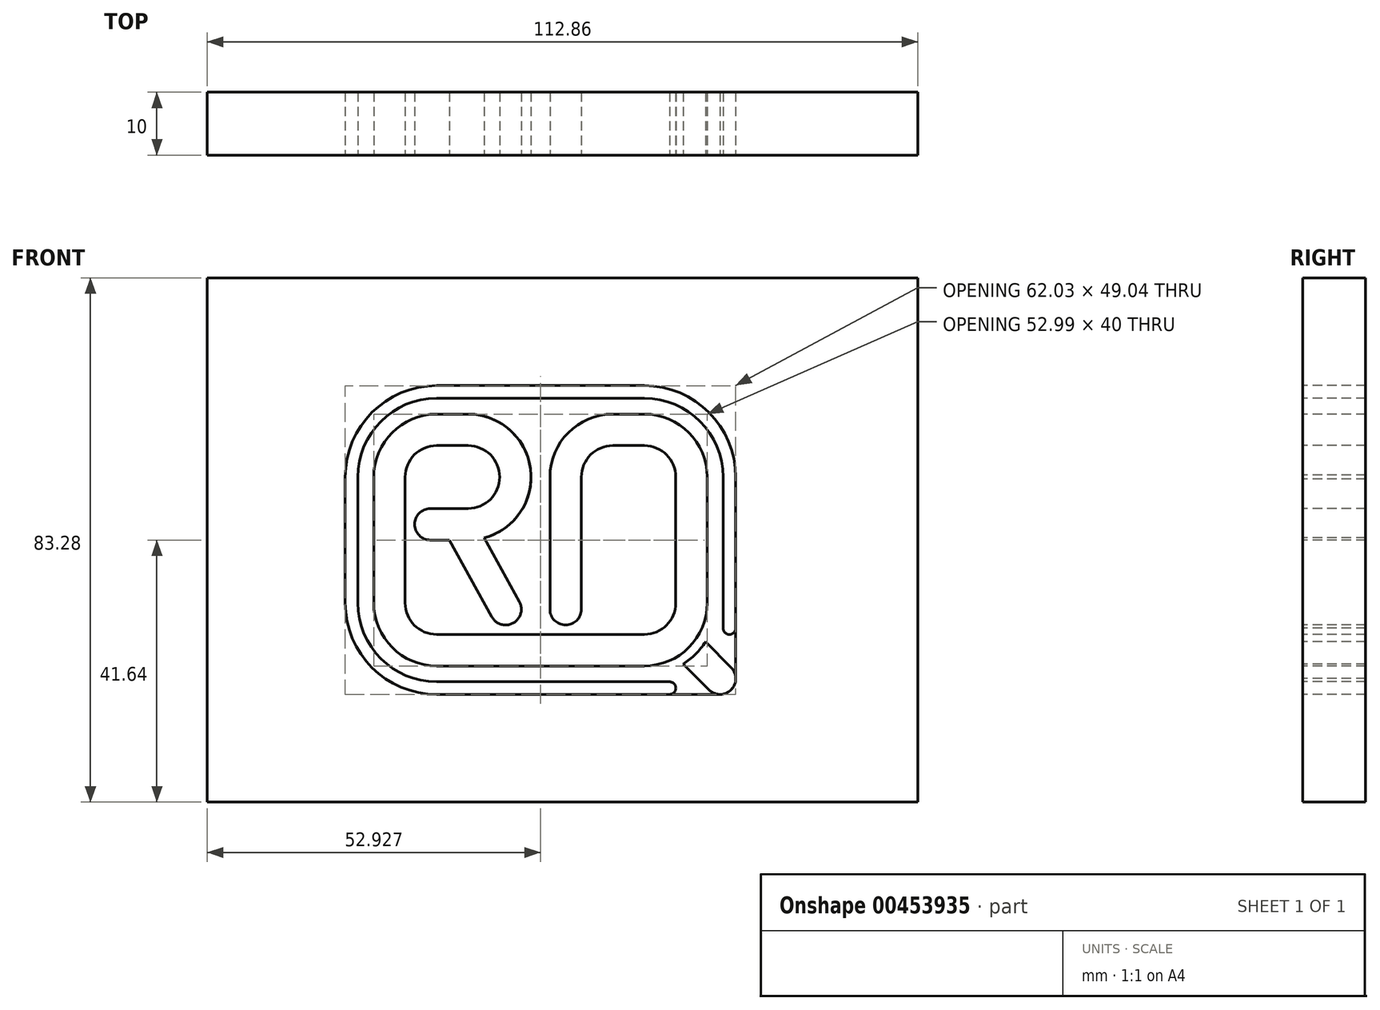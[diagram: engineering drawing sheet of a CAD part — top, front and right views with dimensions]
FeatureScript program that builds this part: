
annotation { "Feature Type Name" : "Feature", "Feature Type Description" : "" }
export const myFeature = defineFeature(function(context is Context, id is Id, definition is map)
    precondition{}
    {
        {
            var Q0;
            Q0=qCreatedBy(makeId("Front.planeOp"),FACE);
            var sketch = newSketch(context, id + "F0", { "sketchPlane" : qUnion([Q0])});
            skPoint(sketch, "E0.middle", {"position": v(0, 0) * mm});
            skLineSegment(sketch, "E1", {"start": v(-25, 10) * mm, "end": v(-25, -10) * mm});
            skLineSegment(sketch, "E2", {"start": v(-2, -20) * mm, "end": v(-0.38, -20) * mm});
            skLineSegment(sketch, "E3", {"start": v(-2, -11) * mm, "end": v(-2, 10) * mm});
            skLineSegment(sketch, "E4", {"start": v(8, 20) * mm, "end": v(13, 20) * mm});
            skLineSegment(sketch, "E5", {"start": v(23, 10) * mm, "end": v(23, -10) * mm});
            skLineSegment(sketch, "E6", {"start": v(13, -20) * mm, "end": v(9, -20) * mm});
            skLineSegment(sketch, "E7", {"start": v(-25, 20) * mm, "end": v(-15, 20) * mm});
            skLineSegment(sketch, "E8", {"start": v(-21, 0) * mm, "end": v(-15, 0) * mm});
            skLineSegment(sketch, "E9", {"start": v(-5, 10.33) * mm, "end": v(-5, 10.33) * mm});
            skPoint(sketch, "E10.visualSharp", {"position": v(-5.33, 20) * mm});
            skArc(sketch, "E10.filletArc", {"start": v(-5, 10.33) * mm, "mid": v(-8.05, 17.19) * mm, "end": v(-15, 20) * mm});
            skArc(sketch, "E11.filletArc", {"start": v(-15, 0) * mm, "mid": v(-7.81, 3.05) * mm, "end": v(-5, 10.33) * mm});
            skPoint(sketch, "E12.visualSharp", {"position": v(-3.63, -20) * mm});
            skPoint(sketch, "E13.visualSharp", {"position": v(23, -20) * mm});
            skArc(sketch, "E13.filletArc", {"start": v(13, -20) * mm, "mid": v(20.07, -17.07) * mm, "end": v(23, -10) * mm});
            skPoint(sketch, "E14.visualSharp", {"position": v(23, 20) * mm});
            skArc(sketch, "E14.filletArc", {"start": v(23, 10) * mm, "mid": v(20.07, 17.07) * mm, "end": v(13, 20) * mm});
            skPoint(sketch, "E15.visualSharp", {"position": v(-2, 20) * mm});
            skArc(sketch, "E15.filletArc", {"start": v(8, 20) * mm, "mid": v(0.92, 17.07) * mm, "end": v(-2, 10) * mm});
            skPoint(sketch, "E16.visualSharp", {"position": v(-2, -20) * mm});
            skArc(sketch, "E17.0", {"start": v(8, 15) * mm, "mid": v(4.46, 13.54) * mm, "end": v(3, 10) * mm});
            skLineSegment(sketch, "E17.1", {"start": v(3, -11) * mm, "end": v(3, 10) * mm});
            skLineSegment(sketch, "E17.2", {"start": v(8, 15) * mm, "end": v(13, 15) * mm});
            skArc(sketch, "E17.4", {"start": v(18, 10) * mm, "mid": v(16.53, 13.54) * mm, "end": v(13, 15) * mm});
            skLineSegment(sketch, "E17.5", {"start": v(18, 10) * mm, "end": v(18, -10) * mm});
            skArc(sketch, "E17.6", {"start": v(13, -15) * mm, "mid": v(16.53, -13.54) * mm, "end": v(18, -10) * mm});
            skLineSegment(sketch, "E17.7", {"start": v(13, -15) * mm, "end": v(9, -15) * mm});
            skArc(sketch, "E18.1", {"start": v(-15, 5) * mm, "mid": v(-11.44, 6.5) * mm, "end": v(-10, 10.08) * mm});
            skArc(sketch, "E18.2", {"start": v(-10, 10.08) * mm, "mid": v(-11.5, 13.56) * mm, "end": v(-15, 15) * mm});
            skLineSegment(sketch, "E18.3", {"start": v(-20, 15) * mm, "end": v(-15, 15) * mm});
            skLineSegment(sketch, "E19.0", {"start": v(-30, 17.5) * mm, "end": v(-30, -10) * mm});
            skLineSegment(sketch, "E20.0", {"start": v(-1, -15) * mm, "end": v(-0.38, -15) * mm});
            skLineSegment(sketch, "E21", {"start": v(-20, -20) * mm, "end": v(-2, -20) * mm});
            skLineSegment(sketch, "E22", {"start": v(-1, -15) * mm, "end": v(9, -15) * mm});
            skLineSegment(sketch, "E23.0", {"start": v(-20, -15) * mm, "end": v(0, -15) * mm});
            skLineSegment(sketch, "E24", {"start": v(-5, 10.33) * mm, "end": v(-5, 0) * mm});
            skLineSegment(sketch, "E25", {"start": v(0.5, -13.5) * mm, "end": v(0.5, -13.5) * mm});
            skPoint(sketch, "E26.visualSharp", {"position": v(3, -13.5) * mm});
            skArc(sketch, "E26.filletArc", {"start": v(0.5, -13.5) * mm, "mid": v(2.26, -12.77) * mm, "end": v(3, -11) * mm});
            skPoint(sketch, "E27.newPointB", {"position": v(-23.5, -13.5) * mm});
            skArc(sketch, "E27.filletArc", {"start": v(-2, -11) * mm, "mid": v(-1.27, -12.77) * mm, "end": v(0.5, -13.5) * mm});
            skPoint(sketch, "E28.visualSharp", {"position": v(-30, -20) * mm});
            skArc(sketch, "E28.filletArc", {"start": v(-30, -19.5) * mm, "mid": v(-29.85, -19.85) * mm, "end": v(-29.5, -20) * mm});
            skLineSegment(sketch, "E29", {"start": v(-7.28, -12.77) * mm, "end": v(-7.28, -12.77) * mm});
            skArc(sketch, "E30.filletArc", {"start": v(-7.28, -12.77) * mm, "mid": v(-6.55, -11) * mm, "end": v(-7.27, -9.24) * mm});
            skArc(sketch, "E31.filletArc", {"start": v(-11.23, -12.21) * mm, "mid": v(-9.4, -13.48) * mm, "end": v(-7.28, -12.77) * mm});
            skLineSegment(sketch, "E32.0", {"start": v(19.16, -19.7) * mm, "end": v(23.25, -23.79) * mm});
            skLineSegment(sketch, "E33.0", {"start": v(22.7, -16.17) * mm, "end": v(26.78, -20.25) * mm});
            skLineSegment(sketch, "E34.0", {"start": v(14.76, -15.3) * mm, "end": v(14.29, -14.83) * mm});
            skPoint(sketch, "E35.newPointB", {"position": v(-25, 20) * mm});
            skPoint(sketch, "E36.visualSharp", {"position": v(-23.5, 5) * mm});
            skPoint(sketch, "E37.visualSharp", {"position": v(-23.5, 0) * mm});
            skLineSegment(sketch, "E38", {"start": v(-30, 10) * mm, "end": v(-30, 17.5) * mm});
            skLineSegment(sketch, "E39", {"start": v(-20, 20) * mm, "end": v(-25, 20) * mm});
            skPoint(sketch, "E40.visualSharp", {"position": v(-30, 20) * mm});
            skArc(sketch, "E40.filletArc", {"start": v(-20, 20) * mm, "mid": v(-27.07, 17.07) * mm, "end": v(-30, 10) * mm});
            skArc(sketch, "E41", {"start": v(23.25, -23.79) * mm, "mid": v(26.78, -23.79) * mm, "end": v(26.78, -20.25) * mm});
            skPoint(sketch, "E42", {"position": v(20.07, -17.07) * mm});
            skPoint(sketch, "E43.orphan", {"position": v(16.53, -13.54) * mm});
            skLineSegment(sketch, "E44.trimOffspring", {"start": v(13, -20) * mm, "end": v(-0.38, -20) * mm});
            skArc(sketch, "E45.trimOffspring", {"start": v(19.16, -19.7) * mm, "mid": v(21.13, -18.13) * mm, "end": v(22.7, -16.17) * mm});
            skPoint(sketch, "E46.newPointB", {"position": v(-25, -20) * mm});
            skArc(sketch, "E46.filletArc", {"start": v(-25, -10) * mm, "mid": v(-23.54, -13.54) * mm, "end": v(-20, -15) * mm});
            skLineSegment(sketch, "E47", {"start": v(-15, 20) * mm, "end": v(8, 20) * mm});
            skLineSegment(sketch, "E48", {"start": v(21.86, -24.52) * mm, "end": v(-20, -24.52) * mm});
            skLineSegment(sketch, "E49", {"start": v(27.51, -22.02) * mm, "end": v(27.51, -18.86) * mm});
            skLineSegment(sketch, "E50", {"start": v(13, 24.52) * mm, "end": v(-20, 24.52) * mm});
            skLineSegment(sketch, "E51", {"start": v(-34.52, -10) * mm, "end": v(-34.52, 10) * mm});
            skPoint(sketch, "E52.orphan", {"position": v(17.43, -17.97) * mm});
            skPoint(sketch, "E53.orphan", {"position": v(13.35, -13.89) * mm});
            skArc(sketch, "E54.0", {"start": v(27.51, 10) * mm, "mid": v(23.26, 20.27) * mm, "end": v(13, 24.52) * mm});
            skArc(sketch, "E55.0", {"start": v(25.51, 10) * mm, "mid": v(21.85, 18.85) * mm, "end": v(13, 22.52) * mm});
            skLineSegment(sketch, "E56.0", {"start": v(25.51, -22.07) * mm, "end": v(25.51, -18.99) * mm});
            skLineSegment(sketch, "E57.0", {"start": v(25.02, -22.52) * mm, "end": v(21.98, -22.52) * mm});
            skLineSegment(sketch, "E58.0", {"start": v(-32.52, -10) * mm, "end": v(-32.52, 10) * mm});
            skLineSegment(sketch, "E59.0", {"start": v(13, 22.52) * mm, "end": v(-20, 22.52) * mm});
            skPoint(sketch, "E60.visualSharp", {"position": v(-32.52, 22.52) * mm});
            skArc(sketch, "E60.filletArc", {"start": v(-20, 22.52) * mm, "mid": v(-28.85, 18.85) * mm, "end": v(-32.52, 10) * mm});
            skArc(sketch, "E61.0", {"start": v(-20, 24.52) * mm, "mid": v(-30.27, 20.27) * mm, "end": v(-34.52, 10) * mm});
            skPoint(sketch, "E62.visualSharp", {"position": v(-32.52, -22.52) * mm});
            skLineSegment(sketch, "E63", {"start": v(26.51, -15) * mm, "end": v(26.51, -16.32) * mm});
            skLineSegment(sketch, "E64.0", {"start": v(18.1, -20.77) * mm, "end": v(22.19, -24.85) * mm, "construction": true});
            skLineSegment(sketch, "E65.0", {"start": v(23.76, -15.1) * mm, "end": v(27.84, -19.2) * mm, "construction": true});
            skArc(sketch, "E66", {"start": v(17, -24.52) * mm, "mid": v(18, -23.52) * mm, "end": v(17, -22.52) * mm});
            skCircle(sketch, "E67", {"center": v(26.51, -14) * mm, "radius": 1 * mm});
            skLineSegment(sketch, "E68.trimOffspring", {"start": v(25.51, -14) * mm, "end": v(25.51, 10) * mm});
            skLineSegment(sketch, "E69.trimOffspring", {"start": v(27.51, -14) * mm, "end": v(27.51, 33) * mm});
            skLineSegment(sketch, "E70.trimOffspring", {"start": v(19.86, -22.52) * mm, "end": v(-20, -22.52) * mm});
            skLineSegment(sketch, "E71", {"start": v(21.86, -24.52) * mm, "end": v(25.02, -24.52) * mm});
            skLineSegment(sketch, "E72", {"start": v(27.51, -14) * mm, "end": v(27.51, -22.02) * mm});
            skLineSegment(sketch, "E73.bottom", {"start": v(-56.43, 41.64) * mm, "end": v(56.43, 41.64) * mm});
            skLineSegment(sketch, "E73.top", {"start": v(-56.43, -41.64) * mm, "end": v(56.43, -41.64) * mm});
            skLineSegment(sketch, "E73.left", {"start": v(-56.43, 41.64) * mm, "end": v(-56.43, -41.64) * mm});
            skLineSegment(sketch, "E73.right", {"start": v(56.43, 41.64) * mm, "end": v(56.43, -41.64) * mm});
            skLineSegment(sketch, "E74", {"start": v(0, 0) * mm, "end": v(0, -38.7) * mm, "construction": true});
            skLineSegment(sketch, "E75", {"start": v(0, 0) * mm, "end": v(33.56, 0) * mm, "construction": true});
            skArc(sketch, "E76.filletArc", {"start": v(-20, 15) * mm, "mid": v(-23.54, 13.54) * mm, "end": v(-25, 10) * mm});
            skArc(sketch, "E77.0", {"start": v(-30, -10) * mm, "mid": v(-27.07, -17.07) * mm, "end": v(-20, -20) * mm});
            skArc(sketch, "E78.0", {"start": v(-34.52, -10) * mm, "mid": v(-30.27, -20.27) * mm, "end": v(-20, -24.52) * mm});
            skArc(sketch, "E79.0", {"start": v(-32.52, -10) * mm, "mid": v(-28.85, -18.85) * mm, "end": v(-20, -22.52) * mm});
            skLineSegment(sketch, "E80", {"start": v(-15, 5) * mm, "end": v(-21, 5) * mm});
            skLineSegment(sketch, "E81", {"start": v(-23.5, 2.5) * mm, "end": v(-23.5, 2.5) * mm});
            skArc(sketch, "E82.filletArc", {"start": v(-21, 5) * mm, "mid": v(-22.77, 4.27) * mm, "end": v(-23.5, 2.5) * mm});
            skArc(sketch, "E83.filletArc", {"start": v(-23.5, 2.5) * mm, "mid": v(-22.77, 0.73) * mm, "end": v(-21, 0) * mm});
            skLineSegment(sketch, "E84", {"start": v(-11.23, -12.21) * mm, "end": v(-18, 0) * mm});
            skPoint(sketch, "E85.startSnap0", {"position": v(-6.55, -11) * mm});
            skLineSegment(sketch, "E86.0", {"start": v(-6.86, -9.79) * mm, "end": v(-13.63, 2.42) * mm});
            skLineSegment(sketch, "E87", {"start": v(-22.87, 0.84) * mm, "end": v(-10.92, -12.66) * mm, "construction": true});
            skLineSegment(sketch, "E88.0", {"start": v(-19.13, 4.16) * mm, "end": v(-7.17, -9.34) * mm, "construction": true});
            skSolve(sketch);
        }
        {
            var Q0;
            Q0=makeQuery(id+"F0.imprint","IMPRINT",FACE,{"disambiguationData":[TD([[makeQuery(id+"F0.imprint","IMPRINT",EDGE,{"derivedFrom":sQuery(id+"F0.wireOp",EDGE,"E1")}),-1.0]])]});
            var Q1;
            {var subQ6=sQuery(id+"F0.wireOp",EDGE,"8dgEX87s-OnN3-UPAw-RyUf-tcfM0RuKeMZf");Q1=makeQuery(id+"F0.imprint","IMPRINT",FACE,{"disambiguationData":[TD([[makeQuery(id+"F0.imprint","IMPRINT",EDGE,{"derivedFrom":subQ6}),1.0]])]});}
            var Q2;
            {var subQ0=sQuery(id+"F0.wireOp",EDGE,"E41");var subQ1=makeQuery(id+"F0.imprint","INTERSECT",VERTEX,{"derivedFrom":[sQuery(id+"F0.wireOp",EDGE,"E33.0"),subQ0]});Q2=makeQuery(id+"F0.imprint","IMPRINT",FACE,{"disambiguationData":[TD([[makeQuery(id+"F0.imprint","IMPRINT",EDGE,{"disambiguationData":[TD([[subQ1,-1.0]])],"derivedFrom":subQ0}),1.0]])]});}
            var Q3;
            {var subQ1=sQuery(id+"F0.wireOp",EDGE,"E33.0");Q3=makeQuery(id+"F0.imprint","IMPRINT",FACE,{"disambiguationData":[TD([[makeQuery(id+"F0.imprint","IMPRINT",EDGE,{"derivedFrom":subQ1}),-1.0]])]});}
            var Q4;
            {var subQ0=sQuery(id+"F0.wireOp",EDGE,"E0.bottom");Q4=makeQuery(id+"F0.imprint","IMPRINT",FACE,{"disambiguationData":[TD([[makeQuery(id+"F0.imprint","IMPRINT",EDGE,{"derivedFrom":subQ0}),-1.0]])]});}
            var Q5;
            {var subQ0=sQuery(id+"F0.wireOp",EDGE,"E0.bottom");Q5=makeQuery(id+"F0.imprint","IMPRINT",FACE,{"disambiguationData":[TD([[makeQuery(id+"F0.imprint","IMPRINT",EDGE,{"derivedFrom":subQ0}),1.0]])]});}
            var Q6;
            {var subQ0=sQuery(id+"F0.wireOp",EDGE,"E31.filletArc");Q6=makeQuery(id+"F0.imprint","IMPRINT",FACE,{"disambiguationData":[TD([[makeQuery(id+"F0.imprint","IMPRINT",EDGE,{"derivedFrom":subQ0}),1.0]])]});}
            extrude(context, id + "F1", {"entities" : qUnion([Q0, Q1, Q2, Q3, Q4, Q5, Q6]), "oppositeDirection" : true, "depth" : 10 * mm});
        }
        {
            var Q0;
            Q0=makeQuery(id+"F0.imprint","IMPRINT",FACE,{"disambiguationData":[TD([[makeQuery(id+"F0.imprint","IMPRINT",EDGE,{"derivedFrom":sQuery(id+"F0.wireOp",EDGE,"E1")}),1.0]])]});
            var Q1;
            {var subQ16=sQuery(id+"F0.wireOp",EDGE,"E2");Q1=makeQuery(id+"F0.imprint","IMPRINT",FACE,{"disambiguationData":[TD([[makeQuery(id+"F0.imprint","IMPRINT",EDGE,{"derivedFrom":subQ16}),-1.0]])]});}
            extrude(context, id + "F2", {"entities" : qUnion([Q0, Q1]), "oppositeDirection" : true, "depth" : 10 * mm});
        }
        {
            var Q0;
            Q0=makeQuery(id+"F0.imprint","IMPRINT",FACE,{"disambiguationData":[TD([[makeQuery(id+"F0.imprint","IMPRINT",EDGE,{"derivedFrom":sQuery(id+"F0.wireOp",EDGE,"E50")}),1.0]])]});
            var Q1;
            {var subQ0=sQuery(id+"F0.wireOp",EDGE,"E66");var subQ2=makeQuery(id+"F0.imprint","IMPRINT",VERTEX,{"derivedFrom":subQ0});Q1=makeQuery(id+"F0.imprint","IMPRINT",FACE,{"disambiguationData":[TD([[makeQuery(id+"F0.imprint","IMPRINT",EDGE,{"disambiguationData":[TD([[subQ2,-1.0]])],"derivedFrom":subQ0}),1.0]])]});}
            var Q2;
            {var subQ0=sQuery(id+"F0.wireOp",EDGE,"E67");var subQ3=makeQuery(id+"F0.imprint","IMPRINT",VERTEX,{"derivedFrom":subQ0});Q2=makeQuery(id+"F0.imprint","IMPRINT",FACE,{"disambiguationData":[TD([[makeQuery(id+"F0.imprint","IMPRINT",EDGE,{"disambiguationData":[TD([[subQ3,1.0]])],"derivedFrom":subQ0}),1.0]])]});}
            extrude(context, id + "F3", {"entities" : qUnion([Q0, Q1, Q2]), "oppositeDirection" : true, "depth" : 10 * mm});
        }
        {
            var Q0;
            Q0=makeQuery(id+"F0.imprint","IMPRINT",FACE,{"disambiguationData":[TD([[makeQuery(id+"F0.imprint","IMPRINT",EDGE,{"derivedFrom":sQuery(id+"F0.wireOp",EDGE,"E50")}),-1.0]])]});
            extrude(context, id + "F4", {"entities" : qUnion([Q0]), "oppositeDirection" : true, "depth" : 10 * mm});
        }
    });
